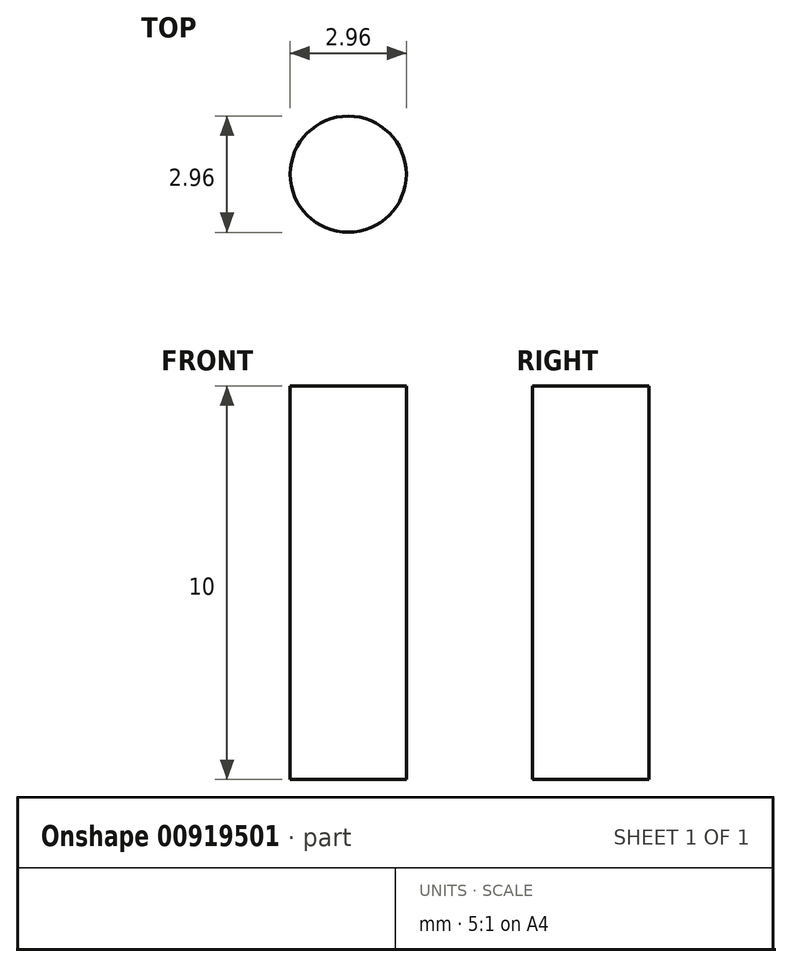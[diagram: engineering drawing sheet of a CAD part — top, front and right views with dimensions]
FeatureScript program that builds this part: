
annotation { "Feature Type Name" : "Feature", "Feature Type Description" : "" }
export const myFeature = defineFeature(function(context is Context, id is Id, definition is map)
    precondition{}
    {
        {
            var Q0;
            Q0=qCreatedBy(makeId("Top.planeOp"),FACE);
            var sketch = newSketch(context, id + "F0", { "sketchPlane" : qUnion([Q0])});
            skCircle(sketch, "E0", {"center": v(0, 0) * mm, "radius": 1.48 * mm});
            skSolve(sketch);
        }
        {
            var Q0;
            Q0 = qSketchRegion(id + "F0", true);
            var Q1;
            Q1=makeQuery(id+"F0.imprint","IMPRINT",FACE,{"disambiguationData":[TD([[makeQuery(id+"F0.imprint","IMPRINT",EDGE,{"derivedFrom":sQuery(id+"F0.wireOp",EDGE,"E0")}),1.0]])]});
            extrude(context, id + "F1", {"entities" : qUnion([Q0, Q1]), "depth" : 10 * mm, "offsetDistance" : 25 * mm});
        }
    });
